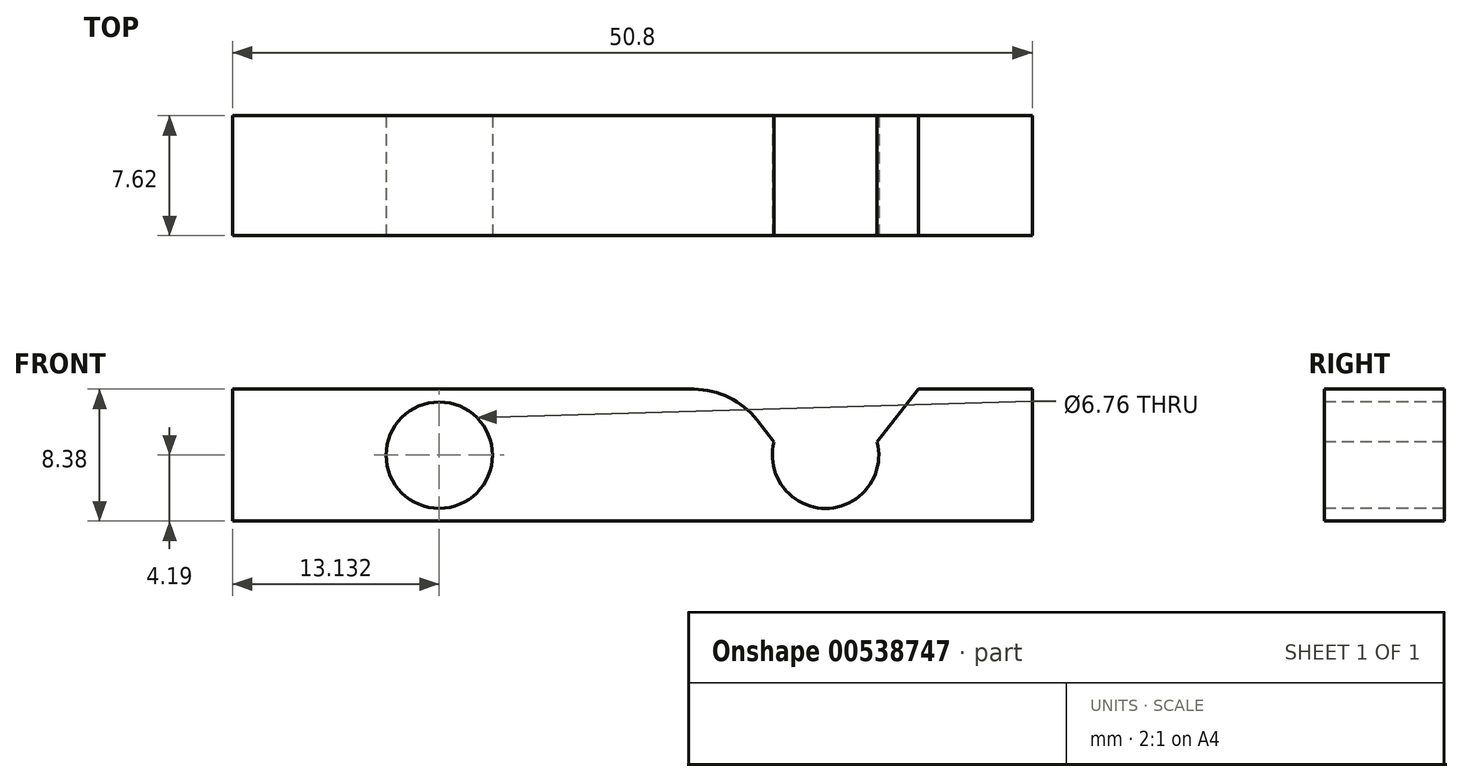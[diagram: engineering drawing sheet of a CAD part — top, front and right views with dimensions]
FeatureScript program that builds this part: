
annotation { "Feature Type Name" : "Feature", "Feature Type Description" : "" }
export const myFeature = defineFeature(function(context is Context, id is Id, definition is map)
    precondition{}
    {
        {
            var Q0;
            Q0=qCreatedBy(makeId("Front.planeOp"),FACE);
            var sketch = newSketch(context, id + "F0", { "sketchPlane" : qUnion([Q0])});
            skLineSegment(sketch, "E0.bottom", {"start": v(25.4, -4.2) * mm, "end": v(-25.4, -4.2) * mm});
            skLineSegment(sketch, "E0.top", {"start": v(25.4, 4.2) * mm, "end": v(-25.4, 4.2) * mm});
            skLineSegment(sketch, "E0.left", {"start": v(25.4, -4.2) * mm, "end": v(25.4, 4.2) * mm});
            skLineSegment(sketch, "E0.right", {"start": v(-25.4, -4.2) * mm, "end": v(-25.4, 4.2) * mm});
            skPoint(sketch, "E0.middle", {"position": v(0, 0) * mm});
            skSolve(sketch);
        }
        {
            var Q0;
            Q0=makeQuery(id+"F0.imprint","IMPRINT",FACE,{"disambiguationData":[TD([[makeQuery(id+"F0.imprint","IMPRINT",EDGE,{"derivedFrom":sQuery(id+"F0.wireOp",EDGE,"E0.bottom")}),-1.0]])]});
            extrude(context, id + "F1", {"entities" : qUnion([Q0]), "depth" : 7.62 * mm, "offsetDistance" : 25.4 * mm});
        }
        {
            var Q0;
            Q0=makeQuery(id+"F1.opExtrude","CAP_FACE",FACE,{"disambiguationData":[OSD([sQuery(id+"F0.wireOp",EDGE,"E0.bottom"),sQuery(id+"F0.wireOp",EDGE,"E0.top"),sQuery(id+"F0.wireOp",EDGE,"E0.left"),sQuery(id+"F0.wireOp",EDGE,"E0.right")])],"isStart":false});
            var sketch = newSketch(context, id + "F2", { "sketchPlane" : qUnion([Q0])});
            skPoint(sketch, "E1", {"position": v(-12.27, 0) * mm});
            skPoint(sketch, "E2.MirrorP", {"position": v(12.27, 0) * mm});
            skSolve(sketch);
        }
        {
            var Q0;
            Q0=sQuery(id+"F2.wireOp",VERTEX,"E1");
            var Q1;
            Q1=sQuery(id+"F2.wireOp",VERTEX,"E2.MirrorP");
            var Q2;
            Q2=makeQuery(id+"F1.opExtrude","SWEPT_BODY",BODY,{"disambiguationData":[OSD([sQuery(id+"F0.wireOp",EDGE,"E0.bottom"),sQuery(id+"F0.wireOp",EDGE,"E0.top"),sQuery(id+"F0.wireOp",EDGE,"E0.left"),sQuery(id+"F0.wireOp",EDGE,"E0.right")])]});
            hole(context, id + "F3", {"style" : HoleStyle.SIMPLE, "endStyle" : HoleEndStyle.BLIND, "standardTappedOrClearance" : lookupTablePath({ "standard" : "ANSI", "fit" : "Normal (ASME)", "size" : "1/4", "type" : "Clearance" }), "standardBlindInLast" : lookupTablePath({ "fit" : "Free", "standard" : "ANSI", "size" : "1/4", "type" : "Clearance" }), "holeDiameter" : 6.76 * mm, "holeDepth" : 23.34 * mm, "tappedDepth" : 19.53 * mm, "tapClearance" : 3, "startFromSketch" : true, "locations" : qUnion([Q0, Q1]), "scope" : qUnion([Q2])});
        }
        {
            var Q0;
            Q0=makeQuery(id+"F1.opExtrude","CAP_FACE",FACE,{"disambiguationData":[OSD([sQuery(id+"F0.wireOp",EDGE,"E0.bottom"),sQuery(id+"F0.wireOp",EDGE,"E0.top"),sQuery(id+"F0.wireOp",EDGE,"E0.left"),sQuery(id+"F0.wireOp",EDGE,"E0.right")])],"isStart":false});
            var sketch = newSketch(context, id + "F4", { "sketchPlane" : qUnion([Q0])});
            skLineSegment(sketch, "E3", {"start": v(12.27, -3.38) * mm, "end": v(6.39, 4.2) * mm});
            skLineSegment(sketch, "E4", {"start": v(6.39, 4.2) * mm, "end": v(18.15, 4.2) * mm});
            skLineSegment(sketch, "E5", {"start": v(18.15, 4.2) * mm, "end": v(12.27, -3.38) * mm});
            skSolve(sketch);
        }
        {
            var Q0;
            {var subQ0=sQuery(id+"F4.wireOp",EDGE,"E4");Q0=makeQuery(id+"F4.imprint","IMPRINT",FACE,{"disambiguationData":[TD([[makeQuery(id+"F4.imprint","IMPRINT",EDGE,{"derivedFrom":subQ0}),1.0]])]});}
            extrude(context, id + "F5", {"entities" : qUnion([Q0]), "operationType" : NewBodyOperationType.REMOVE, "oppositeDirection" : true, "depth" : 25.4 * mm, "offsetDistance" : 25.4 * mm});
        }
        {
            var Q0;
            Q0=makeQuery(id+"F5.boolean.opBoolean","COPY",EDGE,{"derivedFrom":makeQuery(id+"F5.opExtrude","SWEPT_EDGE",EDGE,{"disambiguationData":[OSD([sQuery(id+"F3.hole-1.sketch.wireOp",EDGE,"core_line_2"),sQuery(id+"F3.hole-1.sketch.wireOp",EDGE,"core_line_3"),sQuery(id+"F4.wireOp",EDGE,"E3")])]})});
            var Q1;
            Q1=makeQuery(id+"F5.boolean.opBoolean","COPY",EDGE,{"derivedFrom":makeQuery(id+"F5.opExtrude","SWEPT_EDGE",EDGE,{"disambiguationData":[OSD([sQuery(id+"F3.hole-1.sketch.wireOp",EDGE,"core_line_2"),sQuery(id+"F3.hole-1.sketch.wireOp",EDGE,"core_line_3"),sQuery(id+"F4.wireOp",EDGE,"E5")])]})});
            fillet(context, id + "F6", {"entities" : qUnion([Q0, Q1]), "radius" : 5.08 * mm, "tangentPropagation" : true, "allowEdgeOverflow" : false});
        }
    });
